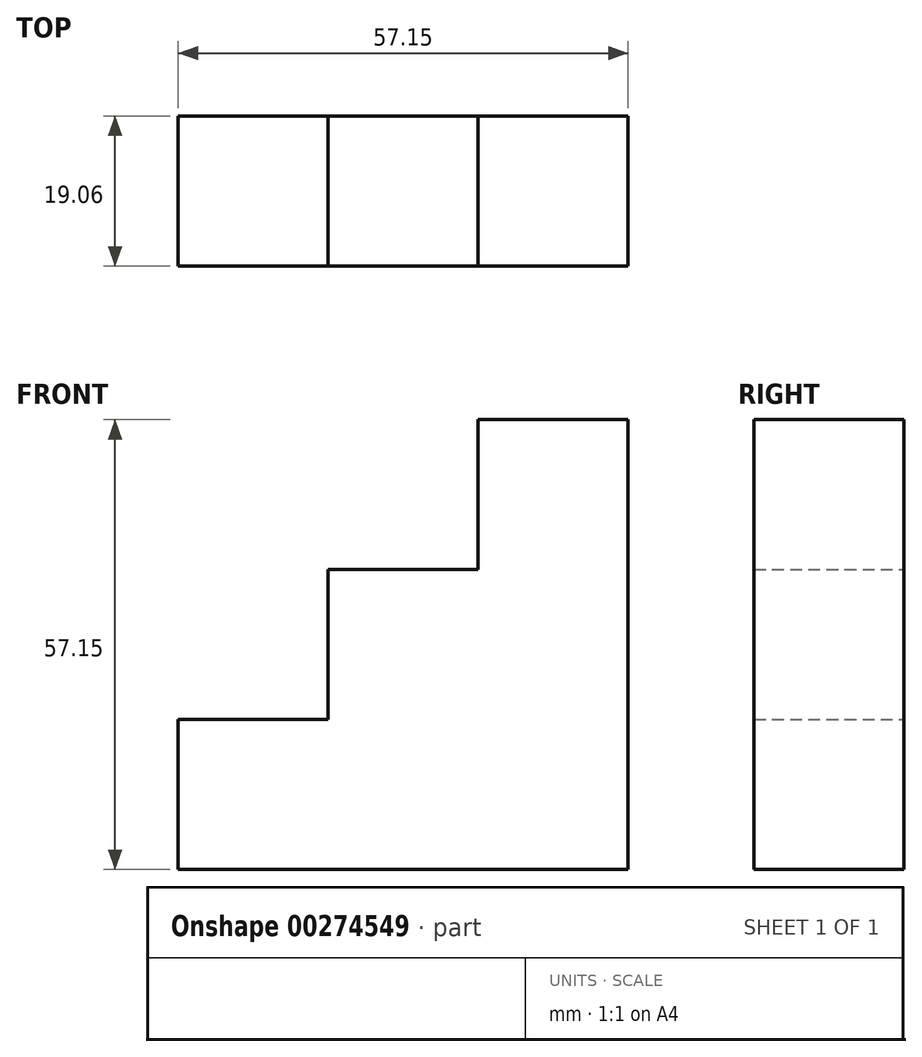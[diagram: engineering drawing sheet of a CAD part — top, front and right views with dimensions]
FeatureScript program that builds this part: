
annotation { "Feature Type Name" : "Feature", "Feature Type Description" : "" }
export const myFeature = defineFeature(function(context is Context, id is Id, definition is map)
    precondition{}
    {
        {
            var Q0;
            Q0=qCreatedBy(makeId("Front.planeOp"),FACE);
            var sketch = newSketch(context, id + "F0", { "sketchPlane" : qUnion([Q0])});
            skLineSegment(sketch, "E0.bottom", {"start": v(-19.05, 19.05) * mm, "end": v(19.05, 19.05) * mm});
            skLineSegment(sketch, "E0.top", {"start": v(-19.05, -19.05) * mm, "end": v(19.05, -19.05) * mm});
            skLineSegment(sketch, "E0.left", {"start": v(-19.05, 19.05) * mm, "end": v(-19.05, -19.05) * mm});
            skLineSegment(sketch, "E0.right", {"start": v(19.05, 19.05) * mm, "end": v(19.05, -19.05) * mm});
            skPoint(sketch, "E0.middle", {"position": v(0, 0) * mm});
            skLineSegment(sketch, "E1.bottom", {"start": v(0, 38.1) * mm, "end": v(19.05, 38.1) * mm});
            skLineSegment(sketch, "E1.top", {"start": v(0, 19.05) * mm, "end": v(19.05, 19.05) * mm});
            skLineSegment(sketch, "E1.left", {"start": v(0, 38.1) * mm, "end": v(0, 19.05) * mm});
            skLineSegment(sketch, "E1.right", {"start": v(19.05, 38.1) * mm, "end": v(19.05, 19.05) * mm});
            skPoint(sketch, "E1.middle", {"position": v(9.53, 28.57) * mm});
            skLineSegment(sketch, "E2.bottom", {"start": v(-19.05, -19.05) * mm, "end": v(0, -19.05) * mm});
            skLineSegment(sketch, "E3.bottom", {"start": v(-38.1, 0.01) * mm, "end": v(-19.05, 0.01) * mm});
            skLineSegment(sketch, "E3.top", {"start": v(-38.1, -19.04) * mm, "end": v(-19.05, -19.04) * mm});
            skLineSegment(sketch, "E3.left", {"start": v(-38.1, 0.01) * mm, "end": v(-38.1, -19.04) * mm});
            skLineSegment(sketch, "E3.right", {"start": v(-19.05, 0.01) * mm, "end": v(-19.05, -19.04) * mm});
            skPoint(sketch, "E3.middle", {"position": v(-28.58, -9.51) * mm});
            skSolve(sketch);
        }
        {
            var Q0;
            Q0 = qSketchRegion(id + "F0", true);
            extrude(context, id + "F1", {"entities" : qUnion([Q0]), "endBound" : BoundingType.SYMMETRIC, "depth" : 19.05 * mm});
        }
    });
